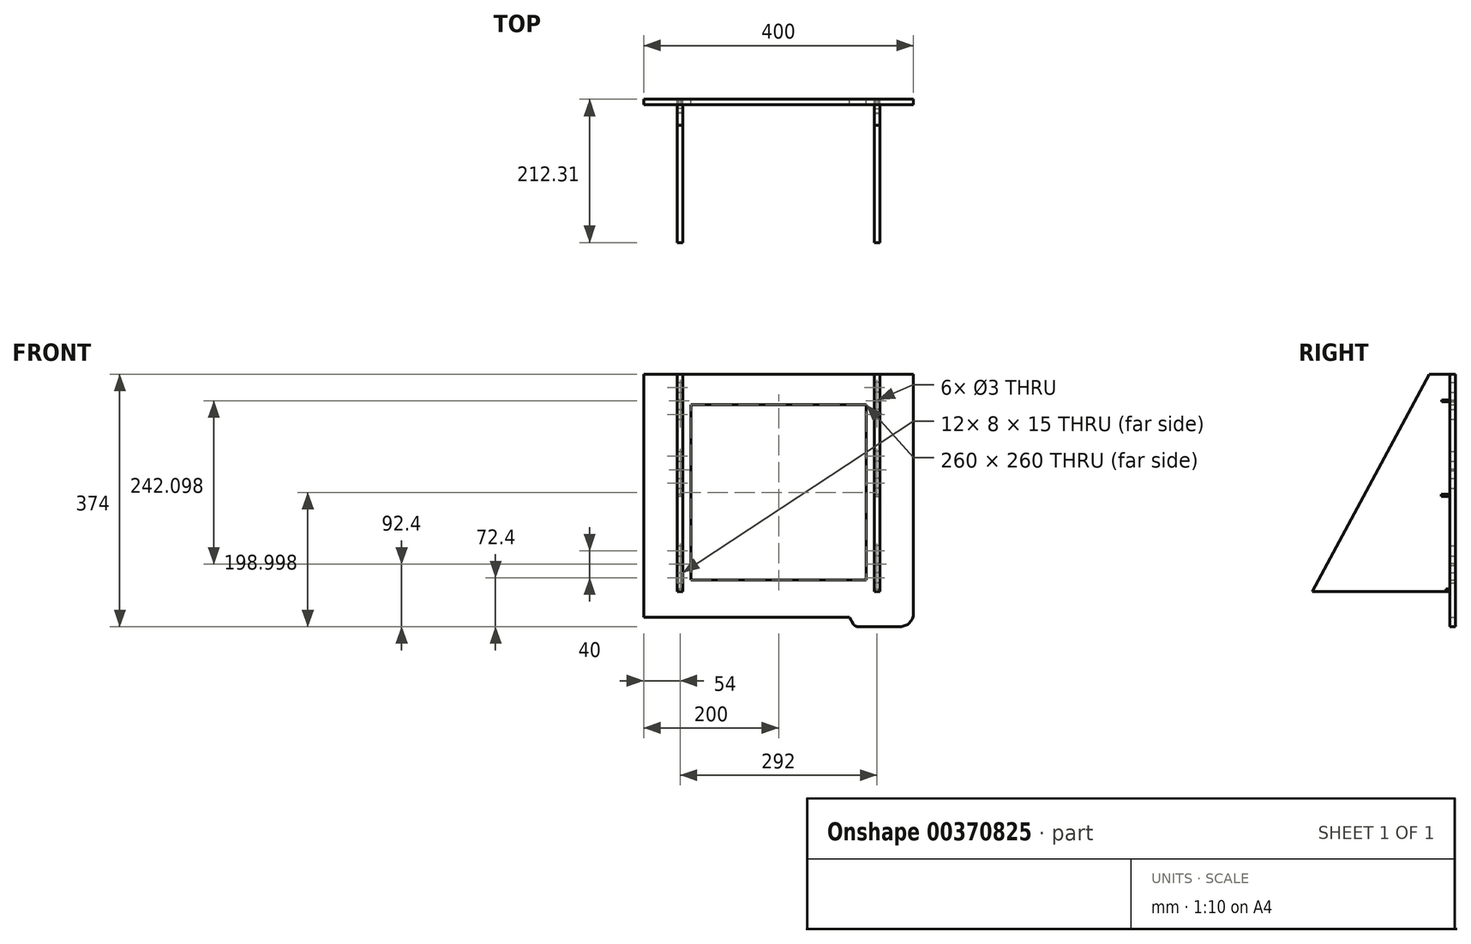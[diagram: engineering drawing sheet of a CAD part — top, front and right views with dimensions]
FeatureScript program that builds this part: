
annotation { "Feature Type Name" : "Feature", "Feature Type Description" : "" }
export const myFeature = defineFeature(function(context is Context, id is Id, definition is map)
    precondition{}
    {
        {
            var Q0;
            Q0=qCreatedBy(makeId("Front.planeOp"),FACE);
            var sketch = newSketch(context, id + "F0", { "sketchPlane" : qUnion([Q0])});
            skLineSegment(sketch, "E0.bottom", {"start": v(-200, 322.1) * mm, "end": v(200, 322.1) * mm});
            skLineSegment(sketch, "E0.top", {"start": v(-200, -37.9) * mm, "end": v(105, -37.9) * mm});
            skLineSegment(sketch, "E0.left", {"start": v(-200, 322.1) * mm, "end": v(-200, -37.9) * mm});
            skLineSegment(sketch, "E0.right", {"start": v(200, 322.1) * mm, "end": v(200, -31.9) * mm});
            skLineSegment(sketch, "E1.bottom", {"start": v(-130, 277.1) * mm, "end": v(130, 277.1) * mm});
            skLineSegment(sketch, "E1.top", {"start": v(-130, 17.1) * mm, "end": v(130, 17.1) * mm});
            skLineSegment(sketch, "E1.left", {"start": v(-130, 277.1) * mm, "end": v(-130, 17.1) * mm});
            skLineSegment(sketch, "E1.right", {"start": v(130, 277.1) * mm, "end": v(130, 17.1) * mm});
            skLineSegment(sketch, "E2", {"start": v(0, 17.1) * mm, "end": v(0, 401.15) * mm, "construction": true});
            skLineSegment(sketch, "E3.bottom", {"start": v(-150, 310.1) * mm, "end": v(-142, 310.1) * mm});
            skLineSegment(sketch, "E3.top", {"start": v(-150, 295.1) * mm, "end": v(-142, 295.1) * mm});
            skLineSegment(sketch, "E3.left", {"start": v(-150, 310.1) * mm, "end": v(-150, 295.1) * mm});
            skLineSegment(sketch, "E3.right", {"start": v(-142, 310.1) * mm, "end": v(-142, 295.1) * mm});
            skPoint(sketch, "E4.firstSnap0", {"position": v(-150, 302.6) * mm});
            skLineSegment(sketch, "E4.bottom", {"start": v(-150, 270.1) * mm, "end": v(-142, 270.1) * mm});
            skLineSegment(sketch, "E4.top", {"start": v(-150, 255.1) * mm, "end": v(-142, 255.1) * mm});
            skLineSegment(sketch, "E4.left", {"start": v(-150, 270.1) * mm, "end": v(-150, 255.1) * mm});
            skLineSegment(sketch, "E4.right", {"start": v(-142, 270.1) * mm, "end": v(-142, 255.1) * mm});
            skCircle(sketch, "E5", {"center": v(-146, 282.6) * mm, "radius": 1.5 * mm});
            skPoint(sketch, "E5.centerSnap0", {"position": v(-146, 270.1) * mm});
            skPoint(sketch, "E6.0.1.0", {"position": v(-150, 200.5) * mm});
            skLineSegment(sketch, "E6.0.1.1", {"start": v(-150, 168) * mm, "end": v(-150, 153) * mm});
            skLineSegment(sketch, "E6.0.1.2", {"start": v(-142, 168) * mm, "end": v(-142, 153) * mm});
            skLineSegment(sketch, "E6.0.1.3", {"start": v(-142, 208) * mm, "end": v(-142, 193) * mm});
            skPoint(sketch, "E6.0.1.4", {"position": v(-146, 168) * mm});
            skLineSegment(sketch, "E6.0.1.5", {"start": v(-150, 208) * mm, "end": v(-150, 193) * mm});
            skCircle(sketch, "E6.0.1.6", {"center": v(-146, 180.5) * mm, "radius": 1.5 * mm});
            skLineSegment(sketch, "E6.0.1.7", {"start": v(-150, 208) * mm, "end": v(-142, 208) * mm});
            skLineSegment(sketch, "E6.0.1.8", {"start": v(-150, 193) * mm, "end": v(-142, 193) * mm});
            skLineSegment(sketch, "E6.0.1.9", {"start": v(-150, 168) * mm, "end": v(-142, 168) * mm});
            skLineSegment(sketch, "E6.0.1.10", {"start": v(-150, 153) * mm, "end": v(-142, 153) * mm});
            skPoint(sketch, "E6.0.2.0", {"position": v(-150, 60.5) * mm});
            skLineSegment(sketch, "E6.0.2.1", {"start": v(-150, 28) * mm, "end": v(-150, 13) * mm});
            skLineSegment(sketch, "E6.0.2.2", {"start": v(-142, 28) * mm, "end": v(-142, 13) * mm});
            skLineSegment(sketch, "E6.0.2.3", {"start": v(-142, 68) * mm, "end": v(-142, 53) * mm});
            skPoint(sketch, "E6.0.2.4", {"position": v(-146, 28) * mm});
            skLineSegment(sketch, "E6.0.2.5", {"start": v(-150, 68) * mm, "end": v(-150, 53) * mm});
            skCircle(sketch, "E6.0.2.6", {"center": v(-146, 40.5) * mm, "radius": 1.5 * mm});
            skLineSegment(sketch, "E6.0.2.7", {"start": v(-150, 68) * mm, "end": v(-142, 68) * mm});
            skLineSegment(sketch, "E6.0.2.8", {"start": v(-150, 53) * mm, "end": v(-142, 53) * mm});
            skLineSegment(sketch, "E6.0.2.9", {"start": v(-150, 28) * mm, "end": v(-142, 28) * mm});
            skLineSegment(sketch, "E6.0.2.10", {"start": v(-150, 13) * mm, "end": v(-142, 13) * mm});
            skLineSegment(sketch, "E7.MirrorCS", {"start": v(150, 168) * mm, "end": v(142, 168) * mm});
            skLineSegment(sketch, "E8.MirrorCS", {"start": v(150, 28) * mm, "end": v(142, 28) * mm});
            skLineSegment(sketch, "E9.MirrorCS", {"start": v(150, 168) * mm, "end": v(150, 153) * mm});
            skLineSegment(sketch, "E10.MirrorCS", {"start": v(150, 68) * mm, "end": v(142, 68) * mm});
            skLineSegment(sketch, "E11.MirrorCS", {"start": v(150, 28) * mm, "end": v(150, 13) * mm});
            skPoint(sketch, "E12.MirrorP", {"position": v(146, 168) * mm});
            skCircle(sketch, "E13.MirrorC", {"center": v(146, 40.5) * mm, "radius": 1.5 * mm});
            skLineSegment(sketch, "E14.MirrorCS", {"start": v(142, 208) * mm, "end": v(142, 193) * mm});
            skLineSegment(sketch, "E15.MirrorCS", {"start": v(150, 153) * mm, "end": v(142, 153) * mm});
            skLineSegment(sketch, "E16.MirrorCS", {"start": v(150, 13) * mm, "end": v(142, 13) * mm});
            skLineSegment(sketch, "E17.MirrorCS", {"start": v(150, 208) * mm, "end": v(142, 208) * mm});
            skLineSegment(sketch, "E18.MirrorCS", {"start": v(150, 193) * mm, "end": v(142, 193) * mm});
            skLineSegment(sketch, "E19.MirrorCS", {"start": v(142, 68) * mm, "end": v(142, 53) * mm});
            skLineSegment(sketch, "E20.MirrorCS", {"start": v(142, 168) * mm, "end": v(142, 153) * mm});
            skPoint(sketch, "E21.MirrorP", {"position": v(150, 200.5) * mm});
            skPoint(sketch, "E22.MirrorP", {"position": v(150, 60.5) * mm});
            skLineSegment(sketch, "E23.MirrorCS", {"start": v(142, 28) * mm, "end": v(142, 13) * mm});
            skLineSegment(sketch, "E24.MirrorCS", {"start": v(150, 68) * mm, "end": v(150, 53) * mm});
            skLineSegment(sketch, "E25.MirrorCS", {"start": v(150, 208) * mm, "end": v(150, 193) * mm});
            skPoint(sketch, "E26.MirrorP", {"position": v(146, 28) * mm});
            skLineSegment(sketch, "E27.MirrorCS", {"start": v(150, 53) * mm, "end": v(142, 53) * mm});
            skCircle(sketch, "E28.MirrorC", {"center": v(146, 180.5) * mm, "radius": 1.5 * mm});
            skLineSegment(sketch, "E29.MirrorCS", {"start": v(150, 270.1) * mm, "end": v(142, 270.1) * mm});
            skCircle(sketch, "E30.MirrorC", {"center": v(146, 282.6) * mm, "radius": 1.5 * mm});
            skLineSegment(sketch, "E31.MirrorCS", {"start": v(142, 270.1) * mm, "end": v(142, 255.1) * mm});
            skLineSegment(sketch, "E32.MirrorCS", {"start": v(150, 270.1) * mm, "end": v(150, 255.1) * mm});
            skPoint(sketch, "E33.MirrorP", {"position": v(146, 270.1) * mm});
            skLineSegment(sketch, "E34.MirrorCS", {"start": v(150, 255.1) * mm, "end": v(142, 255.1) * mm});
            skPoint(sketch, "E35.MirrorP", {"position": v(150, 302.6) * mm});
            skLineSegment(sketch, "E36.MirrorCS", {"start": v(150, 310.1) * mm, "end": v(150, 295.1) * mm});
            skLineSegment(sketch, "E37.MirrorCS", {"start": v(150, 295.1) * mm, "end": v(142, 295.1) * mm});
            skLineSegment(sketch, "E38.MirrorCS", {"start": v(142, 310.1) * mm, "end": v(142, 295.1) * mm});
            skLineSegment(sketch, "E39.MirrorCS", {"start": v(150, 310.1) * mm, "end": v(142, 310.1) * mm});
            skLineSegment(sketch, "E40.top", {"start": v(180, -51.9) * mm, "end": v(117.7, -51.9) * mm});
            skLineSegment(sketch, "E40.right", {"start": v(105, -37.9) * mm, "end": v(110.77, -47.9) * mm});
            skPoint(sketch, "E41.visualSharp", {"position": v(113.08, -51.9) * mm});
            skArc(sketch, "E41.filletArc", {"start": v(110.77, -47.9) * mm, "mid": v(113.7, -50.83) * mm, "end": v(117.7, -51.9) * mm});
            skPoint(sketch, "E42.visualSharp", {"position": v(240, -51.9) * mm});
            skArc(sketch, "E42.filletArc", {"start": v(180, -51.9) * mm, "mid": v(194.14, -46.04) * mm, "end": v(200, -31.9) * mm});
            skSolve(sketch);
        }
        {
            var Q0;
            Q0=makeQuery(id+"F0.imprint","IMPRINT",FACE,{"disambiguationData":[TD([[makeQuery(id+"F0.imprint","IMPRINT",EDGE,{"derivedFrom":sQuery(id+"F0.wireOp",EDGE,"E0.bottom")}),-1.0]])]});
            extrude(context, id + "F1", {"entities" : qUnion([Q0]), "depth" : 8 * mm});
        }
        {
            var Q0;
            Q0=makeQuery(id+"F1.opExtrude","SWEPT_FACE",FACE,{"disambiguationData":[OSD([sQuery(id+"F0.wireOp",EDGE,"E6.0.1.5")])]});
            var sketch = newSketch(context, id + "F2", { "sketchPlane" : qUnion([Q0])});
            skLineSegment(sketch, "E43", {"start": v(0, 322.1) * mm, "end": v(-38.34, 322.1) * mm});
            skLineSegment(sketch, "E44", {"start": v(-38.34, 322.1) * mm, "end": v(-212.31, 0) * mm});
            skLineSegment(sketch, "E45", {"start": v(-212.31, 0) * mm, "end": v(0, 0) * mm});
            skLineSegment(sketch, "E46", {"start": v(0, 282.6) * mm, "end": v(-15.66, 282.6) * mm, "construction": true});
            skLineSegment(sketch, "E47", {"start": v(0, 142.6) * mm, "end": v(-23.94, 142.6) * mm, "construction": true});
            skLineSegment(sketch, "E48", {"start": v(0, 2.6) * mm, "end": v(-19.97, 2.6) * mm, "construction": true});
            skLineSegment(sketch, "E49.bottom", {"start": v(0, 284.1) * mm, "end": v(-20.02, 284.1) * mm});
            skLineSegment(sketch, "E49.top", {"start": v(0, 281.1) * mm, "end": v(-20.02, 281.1) * mm});
            skLineSegment(sketch, "E49.left", {"start": v(0, 284.1) * mm, "end": v(0, 281.1) * mm});
            skLineSegment(sketch, "E49.right", {"start": v(-20.02, 284.1) * mm, "end": v(-20.02, 281.1) * mm});
            skLineSegment(sketch, "E50.bottom", {"start": v(0, 144.1) * mm, "end": v(-20.91, 144.1) * mm});
            skLineSegment(sketch, "E50.top", {"start": v(0, 141.1) * mm, "end": v(-20.91, 141.1) * mm});
            skLineSegment(sketch, "E50.left", {"start": v(0, 144.1) * mm, "end": v(0, 141.1) * mm});
            skLineSegment(sketch, "E50.right", {"start": v(-20.91, 144.1) * mm, "end": v(-20.91, 141.1) * mm});
            skLineSegment(sketch, "E51.bottom", {"start": v(0, 4.1) * mm, "end": v(-13.61, 4.1) * mm});
            skLineSegment(sketch, "E51.top", {"start": v(0, 1.1) * mm, "end": v(-13.61, 1.1) * mm});
            skLineSegment(sketch, "E51.left", {"start": v(0, 4.1) * mm, "end": v(0, 1.1) * mm});
            skLineSegment(sketch, "E51.right", {"start": v(-13.61, 4.1) * mm, "end": v(-13.61, 1.1) * mm});
            skLineSegment(sketch, "E52", {"start": v(0, 322.1) * mm, "end": v(0, 0) * mm});
            skSolve(sketch);
        }
        {
            var Q0;
            {var subQ4=sQuery(id+"F2.wireOp",EDGE,"E43");Q0=makeQuery(id+"F2.imprint","IMPRINT",FACE,{"disambiguationData":[TD([[makeQuery(id+"F2.imprint","IMPRINT",EDGE,{"derivedFrom":subQ4}),1.0]])]});}
            var Q1;
            {var subQ1=sQuery(id+"F0.wireOp",EDGE,"E6.0.1.5");Q1=makeQuery(id+"F2.imprint","IMPRINT",FACE,{"disambiguationData":[TD([[makeQuery(id+"F2.imprint","IMPRINT",EDGE,{"derivedFrom":makeQuery(id+"F1.opExtrude","CAP_EDGE",EDGE,{"disambiguationData":[OSD([subQ1])],"isStart":false})}),1.0]])]});}
            extrude(context, id + "F3", {"entities" : qUnion([Q0, Q1]), "depth" : 8 * mm});
        }
        {
            var Q0;
            Q0=makeQuery(id+"F1.opExtrude","SWEPT_BODY",BODY,{"disambiguationData":[OSD([sQuery(id+"F0.wireOp",EDGE,"E0.bottom"),sQuery(id+"F0.wireOp",EDGE,"E0.top"),sQuery(id+"F0.wireOp",EDGE,"E0.left"),sQuery(id+"F0.wireOp",EDGE,"E0.right"),sQuery(id+"F0.wireOp",EDGE,"E1.bottom"),sQuery(id+"F0.wireOp",EDGE,"E1.top"),sQuery(id+"F0.wireOp",EDGE,"E1.left"),sQuery(id+"F0.wireOp",EDGE,"E1.right"),sQuery(id+"F0.wireOp",EDGE,"E3.bottom"),sQuery(id+"F0.wireOp",EDGE,"E3.top"),sQuery(id+"F0.wireOp",EDGE,"E3.left"),sQuery(id+"F0.wireOp",EDGE,"E3.right"),sQuery(id+"F0.wireOp",EDGE,"E4.bottom"),sQuery(id+"F0.wireOp",EDGE,"E4.top"),sQuery(id+"F0.wireOp",EDGE,"E4.left"),sQuery(id+"F0.wireOp",EDGE,"E4.right"),sQuery(id+"F0.wireOp",EDGE,"E5"),sQuery(id+"F0.wireOp",EDGE,"E6.0.1.1"),sQuery(id+"F0.wireOp",EDGE,"E6.0.1.2"),sQuery(id+"F0.wireOp",EDGE,"E6.0.1.3"),sQuery(id+"F0.wireOp",EDGE,"E6.0.1.5"),sQuery(id+"F0.wireOp",EDGE,"E6.0.1.6"),sQuery(id+"F0.wireOp",EDGE,"E6.0.1.7"),sQuery(id+"F0.wireOp",EDGE,"E6.0.1.8"),sQuery(id+"F0.wireOp",EDGE,"E6.0.1.9"),sQuery(id+"F0.wireOp",EDGE,"E6.0.1.10"),sQuery(id+"F0.wireOp",EDGE,"E6.0.2.1"),sQuery(id+"F0.wireOp",EDGE,"E6.0.2.2"),sQuery(id+"F0.wireOp",EDGE,"E6.0.2.3"),sQuery(id+"F0.wireOp",EDGE,"E6.0.2.5"),sQuery(id+"F0.wireOp",EDGE,"E6.0.2.6"),sQuery(id+"F0.wireOp",EDGE,"E6.0.2.7"),sQuery(id+"F0.wireOp",EDGE,"E6.0.2.8"),sQuery(id+"F0.wireOp",EDGE,"E6.0.2.9"),sQuery(id+"F0.wireOp",EDGE,"E6.0.2.10"),sQuery(id+"F0.wireOp",EDGE,"E7.MirrorCS"),sQuery(id+"F0.wireOp",EDGE,"E8.MirrorCS"),sQuery(id+"F0.wireOp",EDGE,"E9.MirrorCS"),sQuery(id+"F0.wireOp",EDGE,"E10.MirrorCS"),sQuery(id+"F0.wireOp",EDGE,"E11.MirrorCS"),sQuery(id+"F0.wireOp",EDGE,"E13.MirrorC"),sQuery(id+"F0.wireOp",EDGE,"E14.MirrorCS"),sQuery(id+"F0.wireOp",EDGE,"E15.MirrorCS"),sQuery(id+"F0.wireOp",EDGE,"E16.MirrorCS"),sQuery(id+"F0.wireOp",EDGE,"E17.MirrorCS"),sQuery(id+"F0.wireOp",EDGE,"E18.MirrorCS"),sQuery(id+"F0.wireOp",EDGE,"E19.MirrorCS"),sQuery(id+"F0.wireOp",EDGE,"E20.MirrorCS"),sQuery(id+"F0.wireOp",EDGE,"E23.MirrorCS"),sQuery(id+"F0.wireOp",EDGE,"E24.MirrorCS"),sQuery(id+"F0.wireOp",EDGE,"E25.MirrorCS"),sQuery(id+"F0.wireOp",EDGE,"E27.MirrorCS"),sQuery(id+"F0.wireOp",EDGE,"E28.MirrorC"),sQuery(id+"F0.wireOp",EDGE,"E29.MirrorCS"),sQuery(id+"F0.wireOp",EDGE,"E30.MirrorC"),sQuery(id+"F0.wireOp",EDGE,"E31.MirrorCS"),sQuery(id+"F0.wireOp",EDGE,"E32.MirrorCS"),sQuery(id+"F0.wireOp",EDGE,"E34.MirrorCS"),sQuery(id+"F0.wireOp",EDGE,"E36.MirrorCS"),sQuery(id+"F0.wireOp",EDGE,"E37.MirrorCS"),sQuery(id+"F0.wireOp",EDGE,"E38.MirrorCS"),sQuery(id+"F0.wireOp",EDGE,"E39.MirrorCS")])]});
            var Q1;
            Q1=makeQuery(id+"F3.opExtrude","SWEPT_BODY",BODY,{"disambiguationData":[OSD([sQuery(id+"F2.wireOp",EDGE,"E43"),sQuery(id+"F2.wireOp",EDGE,"E44"),sQuery(id+"F2.wireOp",EDGE,"E45"),sQuery(id+"F2.wireOp",EDGE,"E49.bottom"),sQuery(id+"F2.wireOp",EDGE,"E49.top"),sQuery(id+"F2.wireOp",EDGE,"E49.right"),sQuery(id+"F2.wireOp",EDGE,"E50.bottom"),sQuery(id+"F2.wireOp",EDGE,"E50.top"),sQuery(id+"F2.wireOp",EDGE,"E50.right"),sQuery(id+"F2.wireOp",EDGE,"E51.bottom"),sQuery(id+"F2.wireOp",EDGE,"E51.top"),sQuery(id+"F2.wireOp",EDGE,"E51.right"),sQuery(id+"F2.wireOp",EDGE,"E52")])]});
            booleanBodies(context, id + "F4", {"operationType" : BooleanOperationType.SUBTRACTION, "tools" : qUnion([Q0]), "targets" : qUnion([Q1]), "keepTools" : true});
        }
        {
            var Q0;
            Q0=makeQuery(id+"F3.opExtrude","SWEPT_BODY",BODY,{"disambiguationData":[OSD([sQuery(id+"F2.wireOp",EDGE,"E43"),sQuery(id+"F2.wireOp",EDGE,"E44"),sQuery(id+"F2.wireOp",EDGE,"E45"),sQuery(id+"F2.wireOp",EDGE,"E49.bottom"),sQuery(id+"F2.wireOp",EDGE,"E49.top"),sQuery(id+"F2.wireOp",EDGE,"E49.right"),sQuery(id+"F2.wireOp",EDGE,"E50.bottom"),sQuery(id+"F2.wireOp",EDGE,"E50.top"),sQuery(id+"F2.wireOp",EDGE,"E50.right"),sQuery(id+"F2.wireOp",EDGE,"E51.bottom"),sQuery(id+"F2.wireOp",EDGE,"E51.top"),sQuery(id+"F2.wireOp",EDGE,"E51.right"),sQuery(id+"F2.wireOp",EDGE,"E52")])]});
            var Q1;
            Q1=qCreatedBy(makeId("Right.planeOp"),FACE);
            mirror(context, id + "F5", {"entities" : qUnion([Q0]), "mirrorPlane" : qUnion([Q1])});
        }
    });
